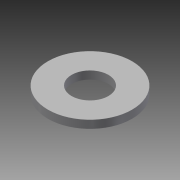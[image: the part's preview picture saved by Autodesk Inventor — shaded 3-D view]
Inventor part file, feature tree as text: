
AUTODESK INVENTOR PART (.ipt)
format: ipt  version: 2014 SP1 (Build 180222100, 222)  size: 74,752 bytes
history: native  units: in
note: dims shown in document units (in); Inventor stores cm internally (conversion verified against a paired STEP export)
features: extrude x1, sketch x1
ambient origin geometry x8: Origin, YZ Plane, XZ Plane, XY Plane, X Axis, Y Axis, Z Axis, Center Point
bodies: Solid1 (feature_tree)
feature tree (2):
  extrude  "Extrusion1"  Depth=0.0469in
  sketch  "Sketch1"  dims[d0=0.2188in d1=0.5in d2=0.0469in d3=0.0in]
